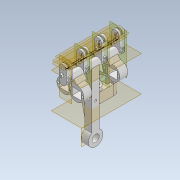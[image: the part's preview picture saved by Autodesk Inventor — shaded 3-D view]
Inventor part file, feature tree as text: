
AUTODESK INVENTOR PART (.ipt)
format: ipt  version: 2020.2 (Build 242310000, 310)  size: 1,037,824 bytes
history: native  units: mm
features: sketch x44, extrude x40, plane x14, mirror x4, chamfer x4, other x3, revolve x1
ambient origin geometry x8: Origin, YZ Plane, XZ Plane, XY Plane, X Axis, Y Axis, Z Axis, Center Point
bodies: Solid1 (feature_tree)
feature tree (110):
  sketch  "Sketch1"  dims[d0=24.0mm d1=24.0mm]
  plane  "Work Plane1"
  plane  "Work Plane3"
  plane  "Work Plane4"
  sketch  "Sketch2"  dims[d2=24.0mm d4=5.0mm]
  extrude  "pinky_joint"  Depth=24.0mm
  extrude  "lock"  Depth=5.0mm
  plane  "Work Plane5"
  mirror  "Mirror1"
  chamfer  "Chamfer1"  Distance=8.0mm
  plane  "Work Plane6"
  revolve  "Revolution2"  [1 undecoded]
  extrude  "pinky_flector_holder"  Depth=6.0mm
  extrude  "finger_union"  Depth=3.0mm TaperAngle=0.0deg
  extrude  "pinky_actuator_hole"  Depth=2.0mm
  plane  "Work Plane7"
  extrude  "ring_base"  Depth=3.0mm
  extrude  "ring_lock"  TaperAngle=180.0deg  [1 undecoded]
  mirror  "Mirror2"
  chamfer  "Chamfer2"  Distance=10.0mm
  plane  "Work Plane8"
  plane  "Work Plane9"
  extrude  "middle_base"  Depth=2.0mm
  plane  "Work Plane11"
  extrude  "index_base"  Depth=5.0mm TaperAngle=0.0deg
  sketch  "Sketch39"  dims[d114=8.0mm d115=0.0mm d116=6.0mm]
  other  "ring_1"
  extrude  "ring_2"  Depth=10.0mm
  extrude  "ring_3"  Depth=6.0mm
  extrude  "ring_4"  Depth=13.962634mm
  other  "middle_1"
  extrude  "middle_2"  Depth=2.0mm TaperAngle=45.0deg
  extrude  "middle_3"  Depth=10.0mm
  extrude  "middle_4"  Depth=8.0mm
  other  "index_1"
  extrude  "index_2"  Depth=8.0mm TaperAngle=0.0deg
  extrude  "index_3"  Depth=2.5mm
  extrude  "index_4"  Depth=3.5mm
  sketch  "Sketch46"  dims[d135=3.5mm d136=2.5mm]
  sketch  "Sketch51"  dims[d137=180.0deg d138=3.5mm]
  extrude  "ring_motor"  TaperAngle=180.0deg  [1 undecoded]
  extrude  "middle_motor"  Depth=5.0mm
  extrude  "index_motor"  Depth=2.0mm
  extrude  "pinky_motor"  Depth=10.0mm TaperAngle=0.0deg
  extrude  "Extrusion48"  Depth=8.0mm
  extrude  "Extrusion50"  Depth=2.0mm
  extrude  "Extrusion46"  Depth=10.0mm TaperAngle=0.0deg
  extrude  "Extrusion52"  Depth=2.5mm
  extrude  "Extrusion54"  Depth=8.0mm TaperAngle=0.0deg
  extrude  "Extrusion55"  Depth=4.0mm
  extrude  "lock_middle"  Depth=2.0mm
  mirror  "Mirror3"
  chamfer  "Chamfer3"  Distance=10.0mm
  extrude  "lock_index"  Depth=5.0mm TaperAngle=0.0deg
  mirror  "Mirror4"
  chamfer  "Chamfer4"  Distance=8.0mm
  extrude  "reinforcement_thread_screw"  Depth=5.0mm
  plane  "Work Plane12"
  extrude  "spine_hand"  Depth=14.0mm TaperAngle=0.0deg
  plane  "Work Plane13"
  extrude  "thumb_motor_"  Depth=14.0mm TaperAngle=0.0deg
  extrude  "Extrusion56"  Depth=14.0mm TaperAngle=0.0deg
  plane  "Work Plane15"
  extrude  "Extrusion57"  Depth=6.0mm
  extrude  "Extrusion43"  Depth=3.0mm TaperAngle=0.0deg
  extrude  "Extrusion44"  Depth=6.0mm
  extrude  "Extrusion45"  TaperAngle=90.0deg  [1 undecoded]
  extrude  "Extrusion58"  Depth=10.0mm
  extrude  "Extrusion59"  Depth=10.0mm
  plane  "Work Plane2"
  sketch  "Sketch18"  dims[d5=8.0mm]
  sketch  "Sketch19"  dims[d6=5.0mm]
  sketch  "Sketch20"  dims[d7=3.0mm]
  sketch  "Sketch22"  dims[d8=10.0mm d15=8.0mm d16=0.0mm]
  sketch  "Sketch23"  dims[d80=15.0mm d81=10.0mm]
  sketch  "Sketch24"  dims[d82=6.0mm d83=3.0mm]
  sketch  "Sketch25"  dims[d84=13.962634mm d85=3.0mm d86=0.0mm]
  sketch  "Sketch26"  dims[d87=3.0mm d88=2.0mm d89=45.0deg d90=3.0mm]
  sketch  "Sketch27"  dims[d92=0.0mm d93=0.0mm d94=3.0mm]
  sketch  "Sketch28"  dims[d95=2.5mm d96=180.0deg]
  plane  "Work Plane10"
  sketch  "Sketch30"  dims[d100=1.0mm]
  sketch  "Sketch31"  dims[d101=2.0mm d102=10.0mm d103=0.0mm]
  sketch  "Sketch34"  dims[d104=4.0mm d105=2.0mm]
  sketch  "Sketch35"  dims[d106=72.0mm d107=0.0mm d110=5.0mm d111=0.0mm]
  sketch  "Sketch36"  dims[d112=3.0mm d113=10.0mm]
  sketch  "Sketch40"  dims[d117=3.0mm d118=13.962634mm]
  sketch  "Sketch41"  dims[d119=3.0mm d120=0.0mm d121=3.0mm d122=2.0mm d123=45.0deg]
  sketch  "Sketch42"  dims[d124=3.0mm d125=10.0mm]
  sketch  "Sketch43"  dims[d126=8.0mm d127=0.0mm d128=3.0mm]
  sketch  "Sketch44"  dims[d129=10.0mm d130=8.0mm d131=0.0mm]
  sketch  "Sketch52"  dims[d139=2.5mm d140=180.0deg]
  sketch  "Sketch53"  dims[d149=5.0mm d150=0.0mm d151=1.0mm]
  sketch  "Sketch54"  dims[d152=4.0mm d153=2.0mm]
  sketch  "Sketch55"  dims[d154=2.0mm d155=10.0mm d156=0.0mm]
  sketch  "Sketch56"  dims[d157=8.0mm d158=0.0mm d159=1.0mm]
  sketch  "Sketch58"  dims[d160=4.0mm d161=2.0mm]
  sketch  "Sketch62"  dims[d162=2.0mm d163=10.0mm d164=0.0mm]
  sketch  "Sketch63"  dims[d165=3.5mm d166=2.5mm]
  sketch  "Sketch64"  dims[d167=180.0deg d168=8.0mm d169=0.0mm]
  sketch  "Sketch65"  dims[d170=1.0mm d171=4.0mm]
  sketch  "Sketch67"  dims[d172=2.0mm d173=2.0mm d174=10.0mm d175=0.0mm]
  sketch  "Sketch69"  dims[d176=8.0mm d177=0.0mm d178=5.0mm d179=0.0mm d180=8.0mm d181=0.0mm]
  sketch  "Sketch71"  dims[d227=15.0mm d230=20.0mm d235=5.0mm d237=9.0mm]
  sketch  "Sketch73"  dims[d238=14.0mm d239=2.0mm d240=0.0mm d241=0.0mm d242=14.0mm d243=2.0mm d244=0.0mm d245=0.0mm]
  sketch  "Sketch74"  dims[d254=5.0mm d257=14.0mm d258=2.0mm d259=0.0mm d260=0.0mm]
  sketch  "Sketch75"  dims[d273=20.0mm d278=14.0mm d279=2.0mm d280=0.0mm d281=0.0mm]
  sketch  "Sketch76"  dims[d282=6.0mm d283=3.0mm]
  sketch  "Sketch77"  dims[d284=13.962634mm d285=3.0mm d286=0.0mm]
  sketch  "Sketch78"  dims[d287=3.0mm d288=2.0mm d289=45.0deg d290=6.0mm d291=90.0deg d292=3.0mm d293=13.962634mm d294=3.0mm d295=0.0mm d296=3.0mm d297=2.0mm d298=45.0deg d299=4.0mm d300=4.0mm d301=4.0mm d302=4.0mm d303=4.0mm d304=4.0mm d305=4.0mm d306=4.0mm d307=2.0mm d308=0.0mm d310=80.0mm d311=0.0mm d312=-48.0mm d320=14.0mm d321=0.0mm d349=4.5mm d350=3.0mm d351=14.987mm d352=0.0mm d353=10.0mm d354=3.0mm d355=35.5mm d356=0.0mm d357=6.0mm d358=120.0deg d359=60.0mm d361=360.0deg d363=2.0mm d364=0.0mm d367=4.5mm d368=0.0mm d369=15.0mm d370=9.0mm d371=6.0mm d372=5.0mm d373=12.0mm d374=10.0mm d375=0.2mm d376=5.0mm d377=3.0mm d378=0.0mm d382=6.0mm d383=5.0mm d384=12.0mm d385=10.0mm d386=0.2mm d387=3.0mm d388=0.0mm d392=15.0mm d393=9.0mm d394=6.0mm d395=5.0mm d396=12.0mm d397=10.0mm d398=0.2mm d399=5.0mm d400=3.0mm d401=0.0mm d405=15.0mm d406=9.0mm d407=5.0mm d408=3.0mm d409=0.0mm d412=3.0mm d413=3.0mm d414=55.0mm d415=0.0mm d416=3.0mm d417=52.0mm d418=0.0mm d428=1.9mm d429=3.0mm d430=1.9mm d431=3.0mm d432=76.0mm d433=0.0mm d434=4.0mm d435=14.0mm d436=10.0mm d437=10.0mm d438=5.0mm d439=5.0mm d440=0.0mm d442=20.0mm d443=20.0mm d444=5.2mm d445=6.2mm d446=5.2mm d447=6.2mm d448=12.4mm d449=10.4mm d450=12.4mm d451=10.4mm d452=20.0mm d453=20.0mm d454=5.0mm d455=10.0mm d456=20.0mm d457=10.0mm d458=0.0mm d459=15.0mm d460=10.0mm d461=0.0mm d77=0.5mm d78=0.872665mm d79=0.5mm d341=0.5mm d342=0.872665mm d343=0.5mm d344=0.872665mm]
note: 4 required parameter values undecoded (feature->parameter linkage not recoverable at this tier; creation-order binding heuristic only, values carry confidence <= 0.55)